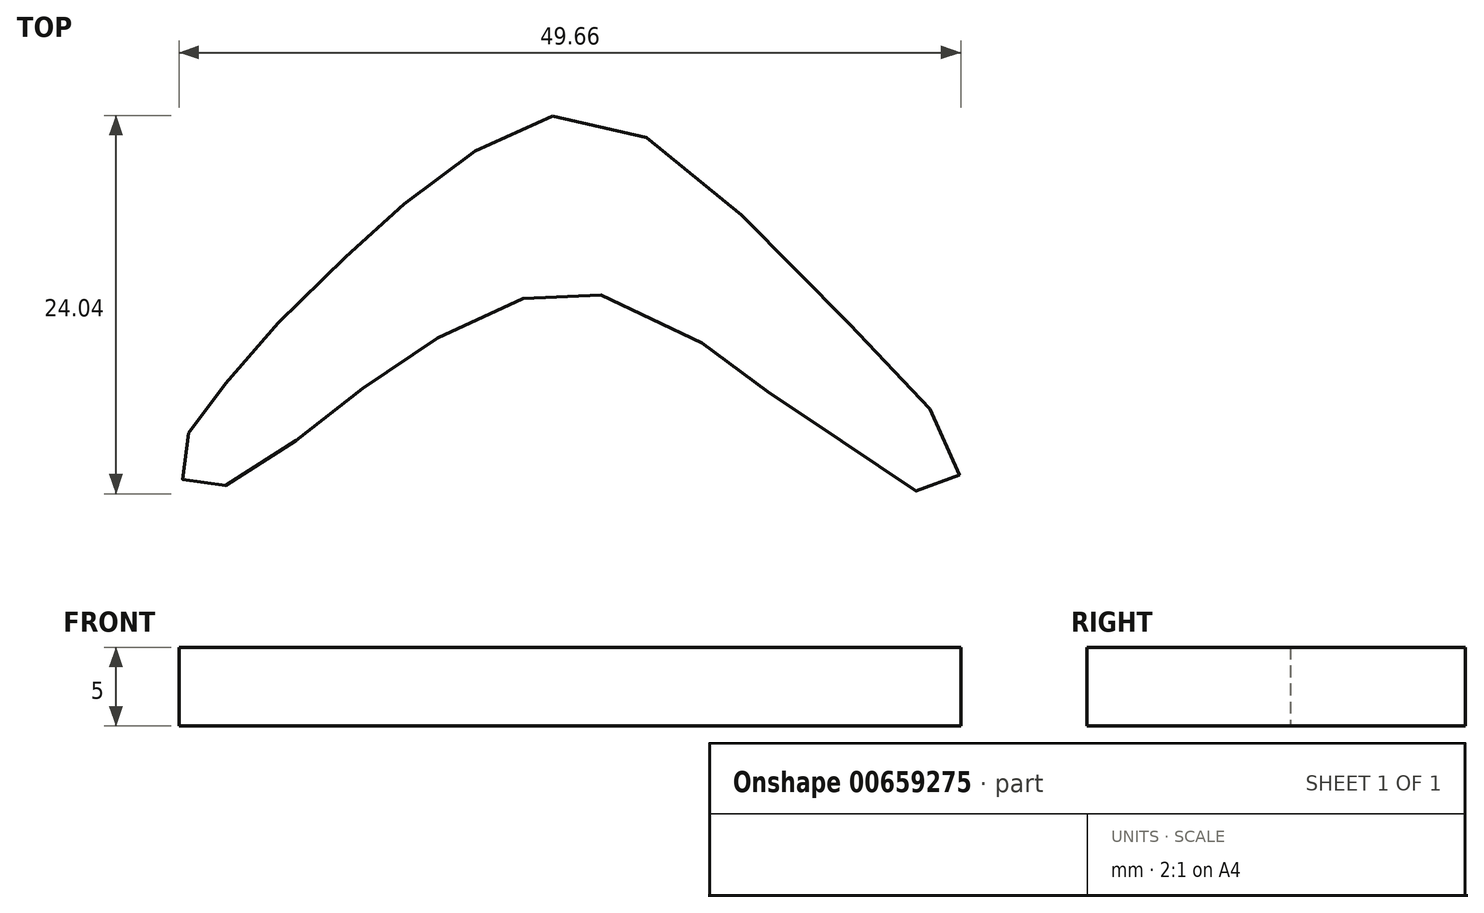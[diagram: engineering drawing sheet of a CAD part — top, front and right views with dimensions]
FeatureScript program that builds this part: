
annotation { "Feature Type Name" : "Feature", "Feature Type Description" : "" }
export const myFeature = defineFeature(function(context is Context, id is Id, definition is map)
    precondition{}
    {
        {
            var Q0;
            Q0=qCreatedBy(makeId("Top.planeOp"),FACE);
            var sketch = newSketch(context, id + "F0", { "sketchPlane" : qUnion([Q0])});
            skFitSpline(sketch, "E0", {"points": [v(-1.34, 16.24) * mm, v(-5.14, 14.74) * mm, v(-9.16, 11.83) * mm, v(-12.1, 9.57) * mm, v(-14.93, 6.83) * mm, v(-18.73, 3.12) * mm, v(-21.38, 0) * mm, v(-23.13, -1.84) * mm, v(-24.37, -3.72) * mm, v(-24.93, -5.43) * mm, v(-25.01, -6.37) * mm, v(-24.11, -7.57) * mm, v(-22.7, -7.57) * mm, v(-21.5, -6.84) * mm, v(-17.36, -4.2) * mm, v(-14.07, -1.63) * mm, v(-10.7, 0.9) * mm, v(-5.65, 3.67) * mm, v(-1.72, 5.04) * mm, v(2.04, 4.78) * mm, v(8.62, 1.53) * mm, v(11.74, -0.86) * mm, v(14.65, -2.74) * mm, v(19.69, -6.33) * mm, v(22.3, -7.74) * mm, v(23.54, -7.48) * mm, v(24.57, -6.37) * mm, v(23.62, -3.68) * mm, v(19.86, 0.64) * mm, v(10.71, 9.91) * mm, v(4, 15.2) * mm, v(-1.34, 16.24) * mm]});
            skSolve(sketch);
        }
        {
            var Q0;
            Q0 = qSketchRegion(id + "F0", true);
            extrude(context, id + "F1", {"entities" : qUnion([Q0]), "depth" : 5 * mm, "offsetDistance" : 25 * mm});
        }
        {
            var Q0;
            Q0=makeQuery(id+"F1.opExtrude","CAP_FACE",FACE,{"disambiguationData":[OSD([sQuery(id+"F0.wireOp",EDGE,"E0")])],"isStart":false});
            var sketch = newSketch(context, id + "F2", { "sketchPlane" : qUnion([Q0])});
            skFitSpline(sketch, "E1", {"points": [v(0, 14.18) * mm, v(-4.72, 12.74) * mm, v(-9.48, 10.08) * mm, v(-15.54, 4.96) * mm, v(-20.38, 0) * mm, v(-23.29, -3.07) * mm, v(-23.98, -4.96) * mm, v(-23.86, -6.4) * mm, v(-22.3, -6.43) * mm, v(-19.47, -4.55) * mm, v(-14.6, -0.98) * mm, v(-8.82, 3.24) * mm, v(-5.95, 4.67) * mm, v(-1.98, 5.98) * mm, v(0, 6.19) * mm, v(0, 6.68) * mm, v(0, 7.62) * mm, v(0, 8.69) * mm, v(0, 9.55) * mm, v(0, 10.45) * mm, v(0, 11.4) * mm, v(0, 12.05) * mm, v(0, 13.36) * mm, v(0, 14.18) * mm]});
            skLineSegment(sketch, "E2", {"start": v(0, 16.27) * mm, "end": v(0, 5.16) * mm});
            skFitSpline(sketch, "E3", {"points": [v(0, 14.18) * mm, v(5.69, 12.54) * mm, v(9.62, 9.22) * mm, v(14.62, 4.71) * mm, v(19.54, 0) * mm, v(22.28, -3.24) * mm, v(22.98, -4.8) * mm, v(22.65, -6.19) * mm, v(20.32, -5.61) * mm, v(14.09, -1.35) * mm, v(7.29, 3.36) * mm, v(2.16, 5.78) * mm, v(0, 6.19) * mm, v(0, 6.68) * mm, v(0, 8) * mm, v(0, 8.69) * mm, v(0, 9.55) * mm, v(0, 10.45) * mm, v(0, 11.4) * mm, v(0, 12.05) * mm, v(0, 13.36) * mm, v(0, 14.18) * mm]});
            skSolve(sketch);
        }
        {
            var Q0;
            {var subQ0=sQuery(id+"F2.wireOp",EDGE,"E2");var subQ1=sQuery(id+"F2.wireOp",EDGE,"E1");var subQ2=makeQuery(id+"F2.imprint","INTERSECT",VERTEX,{"derivedFrom":[subQ1,subQ0]});Q0=makeQuery(id+"F2.imprint","IMPRINT",FACE,{"disambiguationData":[TD([[makeQuery(id+"F2.imprint","IMPRINT",EDGE,{"disambiguationData":[TD([[subQ2,1.0]])],"derivedFrom":subQ0}),-1.0]])]});}
            var Q1;
            {var subQ0=sQuery(id+"F2.wireOp",EDGE,"E3");var subQ2=sQuery(id+"F2.wireOp",EDGE,"E1");var subQ6=makeQuery(id+"F2.imprint","INTERSECT",VERTEX,{"derivedFrom":[subQ2,subQ0]});Q1=makeQuery(id+"F2.imprint","IMPRINT",FACE,{"disambiguationData":[TD([[makeQuery(id+"F2.imprint","IMPRINT",EDGE,{"disambiguationData":[TD([[subQ6,-1.0]])],"derivedFrom":subQ2}),-1.0]])]});}
            extrude(context, id + "F3", {"entities" : qUnion([Q0, Q1]), "operationType" : NewBodyOperationType.REMOVE, "depth" : 3 * mm, "offsetDistance" : 25 * mm});
        }
    });
